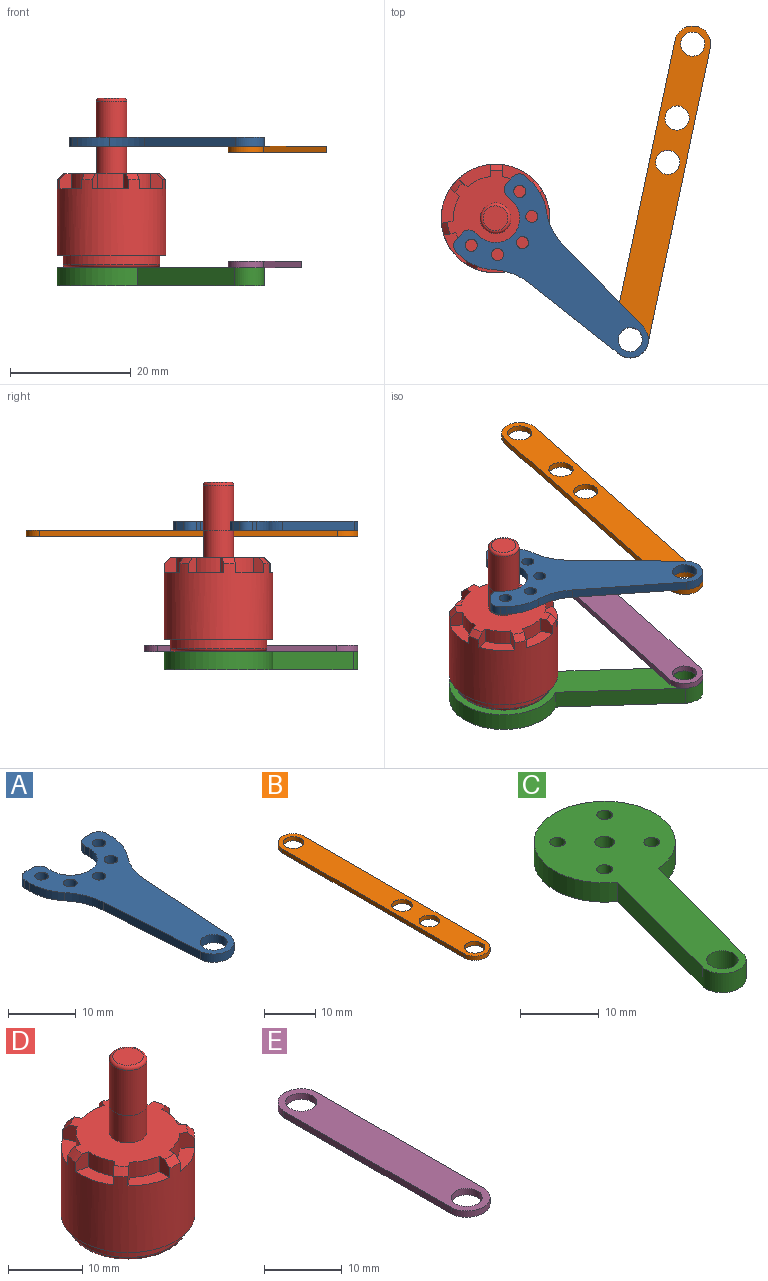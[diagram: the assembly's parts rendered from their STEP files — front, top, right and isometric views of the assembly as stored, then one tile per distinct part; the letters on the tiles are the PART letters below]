
ASSEMBLY  parts=5 mates=5
PART A: 26 faces, bbox 17x35.5x1.5 mm
  f0: plane 19.06x1.5mm, normal (1,-0.07,0), area 28.7mm2, adj f2,f4,f5,f20
  f1: plane 19.06x1.5mm, normal (-1,-0.07,0), area 28.7mm2, adj f2,f4,f5,f21
  f2: cylinder r=3mm len=5.99mm, axis (0,0,-1), area 13.5mm2, adj f0,f1,f4,f5
  f3: cylinder r=2mm len=4mm, axis (0,0,-1), area 18.8mm2, adj f4,f5
  f4: plane 35.5x17mm, normal (0,0,1), area 261.8mm2, adj f0,f1,f2,f3,f6,f7,f8,f9
  f5: plane 35.5x17mm, normal (0,0,-1), area 261.8mm2, adj f0,f1,f2,f3,f6,f7,f8,f9
  f6: cylinder r=8.5mm len=5.42mm, axis (0,0,1), area 8.8mm2, adj f4,f5,f8,f21
  f7: plane 1.5x1.5mm, normal (0,1,0), area 2.3mm2, adj f4,f5,f22,f25
  f8: plane 1.5x1mm, normal (-1,0,0), area 1.5mm2, adj f4,f5,f6,f25
  f9: cylinder r=8.5mm len=5.42mm, axis (0,0,1), area 8.8mm2, adj f4,f5,f10,f20
  f10: plane 1.5x1mm, normal (1,0,0), area 1.5mm2, adj f4,f5,f9,f24
  f11: plane 1.5x1.5mm, normal (0,1,0), area 2.3mm2, adj f4,f5,f23,f24
  f12: plane 1.5x1mm, normal (1,0,0), area 1.5mm2, adj f4,f5,f13,f22
  f13: cylinder r=4mm len=8mm, axis (0,0,1), area 18.8mm2, adj f4,f5,f12,f14
  f14: plane 1.5x1mm, normal (-1,0,0), area 1.5mm2, adj f4,f5,f13,f23
  f15: cylinder r=1mm len=2mm, axis (0,0,1), area 9.4mm2, adj f4,f5
  f16: cylinder r=1mm len=2mm, axis (0,0,1), area 9.4mm2, adj f4,f5
  f17: cylinder r=1mm len=2mm, axis (0,0,1), area 9.4mm2, adj f4,f5
  f18: cylinder r=1mm len=2mm, axis (0,0,1), area 9.4mm2, adj f4,f5
  f19: cylinder r=1mm len=2mm, axis (0,0,1), area 9.4mm2, adj f4,f5
  f20: cylinder r=10mm len=5.71mm, axis (0,0,1), area 9.4mm2, adj f0,f4,f5,f9
  f21: cylinder r=10mm len=5.71mm, axis (0,0,1), area 9.4mm2, adj f1,f4,f5,f6
  f22: cylinder r=1.5mm len=1.5mm, axis (0,0,1), area 3.5mm2, adj f4,f5,f7,f12
  f23: cylinder r=1.5mm len=1.5mm, axis (0,0,1), area 3.5mm2, adj f4,f5,f11,f14
  f24: cylinder r=1.5mm len=1.5mm, axis (0,0,-1), area 3.5mm2, adj f4,f5,f10,f11
  f25: cylinder r=1.5mm len=1.5mm, axis (0,0,-1), area 3.5mm2, adj f4,f5,f7,f8
PART B: 10 faces, bbox 6x56x1 mm
  f0: plane 50.4x1mm, normal (1,0,0), area 50.4mm2, adj f1,f3,f6,f7
  f1: cylinder r=3mm len=5.99mm, axis (0,0,-1), area 9mm2, adj f0,f2,f6,f7
  f2: plane 50.4x1mm, normal (-1,0,0), area 50.4mm2, adj f1,f3,f6,f7
  f3: cylinder r=3mm len=5.99mm, axis (0,0,-1), area 9mm2, adj f0,f2,f6,f7
  f4: cylinder r=2mm len=4mm, axis (0,0,-1), area 12.6mm2, adj f6,f7
  f5: cylinder r=2mm len=4mm, axis (0,0,-1), area 12.6mm2, adj f6,f7
  f6: plane 56x5.99mm, normal (0,0,1), area 277.3mm2, adj f0,f1,f2,f3,f4,f5,f8,f9
  f7: plane 56x5.99mm, normal (0,0,-1), area 277.3mm2, adj f0,f1,f2,f3,f4,f5,f8,f9
  f8: cylinder r=2mm len=4mm, axis (0,0,1), area 12.6mm2, adj f6,f7
  f9: cylinder r=2mm len=4mm, axis (0,0,1), area 12.6mm2, adj f6,f7
PART C: 12 faces, bbox 19.8x41x3 mm
  f0: cylinder r=9mm len=18mm, axis (0,0,1), area 151.3mm2, adj f1,f3,f10,f11
  f1: plane 20.78x5.57mm, normal (0.97,-0.26,0), area 64.5mm2, adj f0,f2,f10,f11
  f2: cylinder r=3mm len=5.9mm, axis (0,0,1), area 28.3mm2, adj f1,f3,f10,f11
  f3: plane 20.78x5.57mm, normal (-0.97,0.26,0), area 64.5mm2, adj f0,f2,f10,f11
  f4: cylinder r=1mm len=3mm, axis (0,0,1), area 18.8mm2, adj f10,f11
  f5: cylinder r=1mm len=3mm, axis (0,0,1), area 18.8mm2, adj f10,f11
  f6: cylinder r=1mm len=3mm, axis (0,0,1), area 18.8mm2, adj f10,f11
  f7: cylinder r=1mm len=3mm, axis (0,0,1), area 18.8mm2, adj f10,f11
  f8: cylinder r=1.25mm len=3mm, axis (0,0,1), area 23.6mm2, adj f10,f11
  f9: cylinder r=2mm len=4mm, axis (0,0,1), area 37.7mm2, adj f10,f11
  f10: plane 40.98x19.76mm, normal (0,0,-1), area 365.6mm2, adj f0,f1,f2,f3,f4,f5,f6,f7
  f11: plane 40.98x19.76mm, normal (0,0,1), area 365.6mm2, adj f0,f1,f2,f3,f4,f5,f6,f7
PART D: 54 faces, bbox 18x18x28 mm
  f0: plane 15x15mm, normal (0,0,-1), area 164.1mm2, adj f41,f46,f48,f50,f52
  f1: cylinder r=2.5mm len=5mm, axis (0,0,-1), area 71.3mm2, adj f3,f43
  f2: cylinder r=9mm len=18mm, axis (0,0,1), area 643.1mm2, adj f4,f6,f7,f8,f10,f11,f12,f14
  f3: plane 15.92x15.59mm, normal (0,0,1), area 148.3mm2, adj f1,f4,f5,f6,f8,f9,f10,f12
  f4: plane 2.51x1.97mm, normal (0.22,0.97,0), area 4.5mm2, adj f2,f3,f5,f7,f33
  f5: cylinder r=7mm len=3.29mm, axis (0,0,1), area 10.7mm2, adj f3,f4,f6,f7
  f6: plane 2.51x1.82mm, normal (-0.9,-0.43,0), area 4.5mm2, adj f2,f3,f5,f7,f38
  f7: plane 5.11x4.59mm, normal (0,0,1), area 10.4mm2, adj f2,f4,f5,f6
  f8: plane 2.51x1.82mm, normal (0.9,-0.43,0), area 4.5mm2, adj f2,f3,f9,f11,f37
  f9: cylinder r=7mm len=3.29mm, axis (0,0,1), area 10.7mm2, adj f3,f8,f10,f11
  f10: plane 2.51x1.97mm, normal (-0.22,0.97,0), area 4.5mm2, adj f2,f3,f9,f11,f36
  f11: plane 5.11x4.59mm, normal (0,0,1), area 10.4mm2, adj f2,f8,f9,f10
  f12: plane 2.51x1.97mm, normal (0.22,-0.97,0), area 4.5mm2, adj f2,f3,f13,f15,f36
  f13: cylinder r=7mm len=4.1mm, axis (0,0,1), area 10.7mm2, adj f3,f12,f14,f15
  f14: plane 2.51x1.58mm, normal (0.62,0.78,0), area 4.5mm2, adj f2,f3,f13,f15,f35
  f15: plane 5.81x2.96mm, normal (0,0,1), area 10.4mm2, adj f2,f12,f13,f14
  f16: plane 2.51x1.58mm, normal (-0.62,-0.78,0), area 4.5mm2, adj f2,f3,f17,f19,f35
  f17: cylinder r=7mm len=3.79mm, axis (0,0,1), area 10.7mm2, adj f3,f16,f18,f19
  f18: plane 2.51x2.02mm, normal (1,0,0), area 4.5mm2, adj f2,f3,f17,f19,f34
  f19: plane 5.37x3.84mm, normal (0,0,1), area 10.4mm2, adj f2,f16,f17,f18
  f20: plane 2.51x2.02mm, normal (-1,0,0), area 4.5mm2, adj f2,f3,f21,f23,f34
  f21: cylinder r=7mm len=3.79mm, axis (0,0,1), area 10.7mm2, adj f3,f20,f22,f23
  f22: plane 2.51x1.58mm, normal (0.62,-0.78,0), area 4.5mm2, adj f2,f3,f21,f23,f32
  f23: plane 5.37x3.84mm, normal (0,0,1), area 10.4mm2, adj f2,f20,f21,f22
  f24: plane 2.51x1.58mm, normal (-0.62,0.78,0), area 4.5mm2, adj f2,f3,f25,f27,f32
  f25: cylinder r=7mm len=4.1mm, axis (0,0,1), area 10.7mm2, adj f3,f24,f26,f27
  f26: plane 2.51x1.97mm, normal (-0.22,-0.97,0), area 4.5mm2, adj f2,f3,f25,f27,f33
  f27: plane 5.81x2.96mm, normal (0,0,1), area 10.4mm2, adj f2,f24,f25,f26
  f28: plane 2.51x1.82mm, normal (0.9,0.43,0), area 4.5mm2, adj f2,f3,f29,f31,f38
  f29: cylinder r=7mm len=4.21mm, axis (0,0,1), area 10.7mm2, adj f3,f28,f30,f31
  f30: plane 2.51x1.82mm, normal (-0.9,0.43,0), area 4.5mm2, adj f2,f3,f29,f31,f37
  f31: plane 5.96x2.32mm, normal (0,0,1), area 10.4mm2, adj f2,f28,f29,f30
  f32: cone r=8mm half-angle=45deg, axis (0,0,-1), area 2.8mm2, adj f2,f3,f22,f24
  f33: cone r=8mm half-angle=45deg, axis (0,0,-1), area 2.8mm2, adj f2,f3,f4,f26
  f34: cone r=8mm half-angle=45deg, axis (0,0,-1), area 2.8mm2, adj f2,f3,f18,f20
  f35: cone r=8mm half-angle=45deg, axis (0,0,-1), area 2.8mm2, adj f2,f3,f14,f16
  f36: cone r=8mm half-angle=45deg, axis (0,0,-1), area 2.8mm2, adj f2,f3,f10,f12
  f37: cone r=8mm half-angle=45deg, axis (0,0,-1), area 2.8mm2, adj f2,f3,f8,f30
  f38: cone r=8mm half-angle=45deg, axis (0,0,-1), area 2.8mm2, adj f2,f3,f6,f28
  f39: cylinder r=8mm len=16mm, axis (0,0,-1), area 75.4mm2, adj f40,f41
  f40: plane 18x18mm, normal (0,0,-1), area 53.4mm2, adj f2,f39
  f41: torus R=7.5mm, axis (0,0,1), area 38.6mm2, adj f0,f39
  f42: cylinder r=2.55mm len=7.46mm, axis (0,0,1), area 119.5mm2, adj f43,f45
  f43: plane 5.1x5.1mm, normal (0,0,-1), area 0.8mm2, adj f1,f42
  f44: plane 4.1x4.1mm, normal (0,0,1), area 13.2mm2, adj f45
  f45: torus R=2.05mm, axis (0,0,1), area 11.7mm2, adj f42,f44
  f46: cylinder r=1mm len=4mm, axis (0,0,-1), area 25.1mm2, adj f0,f47
  f47: plane 2x2mm, normal (0,0,-1), area 3.1mm2, adj f46
  f48: cylinder r=1mm len=4mm, axis (0,0,-1), area 25.1mm2, adj f0,f49
  f49: plane 2x2mm, normal (0,0,-1), area 3.1mm2, adj f48
  f50: cylinder r=1mm len=4mm, axis (0,0,-1), area 25.1mm2, adj f0,f51
  f51: plane 2x2mm, normal (0,0,-1), area 3.1mm2, adj f50
  f52: cylinder r=1mm len=4mm, axis (0,0,-1), area 25.1mm2, adj f0,f53
  f53: plane 2x2mm, normal (0,0,-1), area 3.1mm2, adj f52
PART E: 8 faces, bbox 6x36x1 mm
  f0: plane 30.32x1mm, normal (1,0,0), area 30.3mm2, adj f1,f3,f6,f7
  f1: cylinder r=3mm len=5.99mm, axis (0,0,-1), area 9.1mm2, adj f0,f2,f6,f7
  f2: plane 30.32x1mm, normal (-1,0,0), area 30.3mm2, adj f1,f3,f6,f7
  f3: cylinder r=3mm len=5.99mm, axis (0,0,-1), area 9.1mm2, adj f0,f2,f6,f7
  f4: cylinder r=2mm len=4mm, axis (0,0,-1), area 12.6mm2, adj f6,f7
  f5: cylinder r=2mm len=4mm, axis (0,0,-1), area 12.6mm2, adj f6,f7
  f6: plane 36x5.99mm, normal (0,0,1), area 182.9mm2, adj f0,f1,f2,f3,f4,f5
  f7: plane 36x5.99mm, normal (0,0,-1), area 182.9mm2, adj f0,f1,f2,f3,f4,f5
PLACE A rot(axis=(0,0,1),48deg) t=(8.41,32.83,6.04)mm
PLACE B rot(axis=(0,0,1),168.1deg) t=(34.84,32.33,3.54)mm
PLACE C rot(axis=(0,0,1),63deg) t=(8.41,32.83,-14)mm
PLACE D rot(axis=(0,0,-1),27deg) t=(8.41,32.83,1.5)mm fixed
PLACE E rot(axis=(0,0,1),168.1deg) t=(29.15,5.42,-17)mm
MATE revolute B.f1 <-> A.f2  axis (0,0,1) through (30.7,12.76,6.04)mm
MATE revolute E.f1 <-> C.f2  axis (0,0,-1) through (30.7,12.76,-14)mm
MATE revolute D.f1 <-> A.f6  axis (0,0,-1) through (8.41,32.83,6.04)mm
MATE fastened C.f0 <-> D.f1  axis (0,0,1) through (8.41,32.83,-14)mm
MATE cylindrical E.f3 <-> B.f8  axis (0,0,1) through (36.91,42.11,-13)mm
